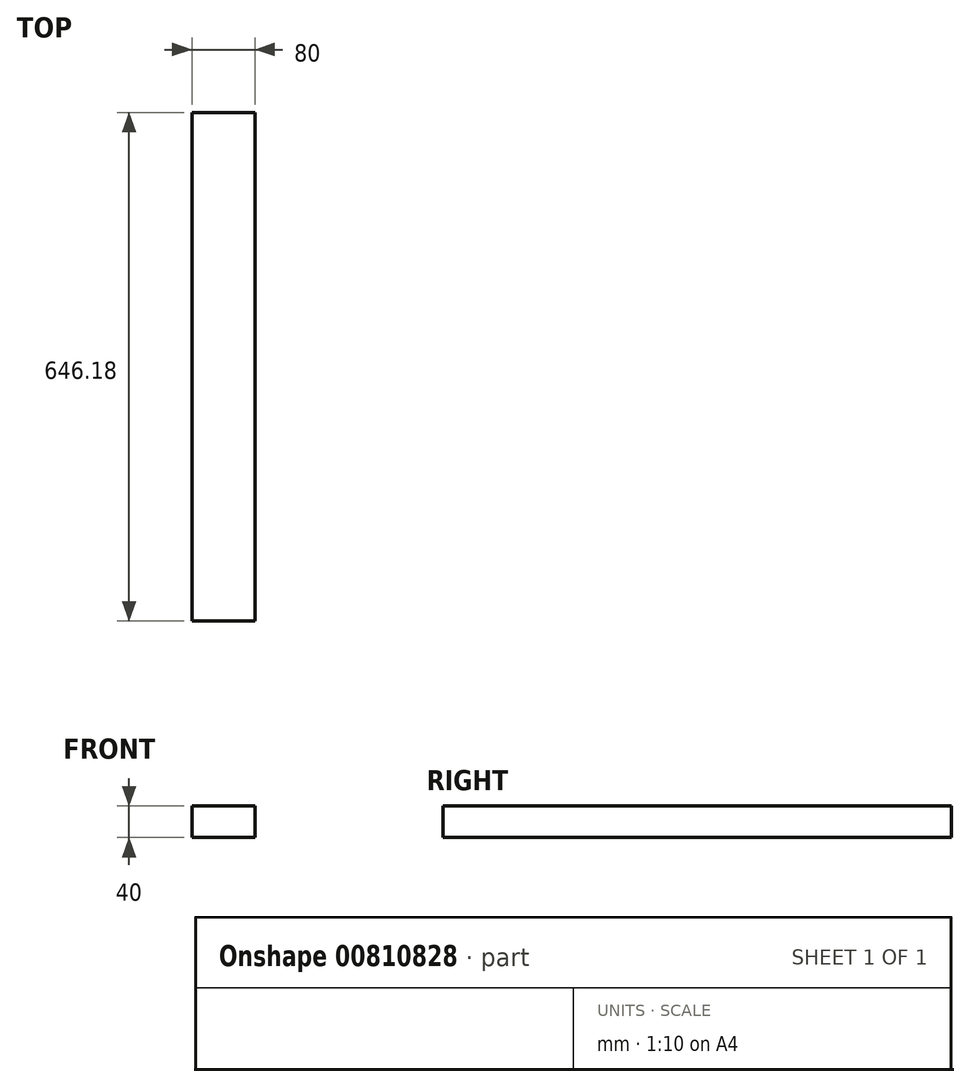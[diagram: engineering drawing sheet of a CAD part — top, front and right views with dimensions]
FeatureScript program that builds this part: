
annotation { "Feature Type Name" : "Feature", "Feature Type Description" : "" }
export const myFeature = defineFeature(function(context is Context, id is Id, definition is map)
    precondition{}
    {
        {
            var Q0;
            Q0=qCreatedBy(makeId("Front.planeOp"),FACE);
            var sketch = newSketch(context, id + "F0", { "sketchPlane" : qUnion([Q0])});
            skLineSegment(sketch, "E0.bottom", {"start": v(-40, 20) * mm, "end": v(40, 20) * mm});
            skLineSegment(sketch, "E0.top", {"start": v(-40, -20) * mm, "end": v(40, -20) * mm});
            skLineSegment(sketch, "E0.left", {"start": v(-40, 20) * mm, "end": v(-40, -20) * mm});
            skLineSegment(sketch, "E0.right", {"start": v(40, 20) * mm, "end": v(40, -20) * mm});
            skPoint(sketch, "E0.middle", {"position": v(0, 0) * mm});
            skSolve(sketch);
        }
        {
            var Q0;
            Q0=makeQuery(id+"F0.imprint","IMPRINT",FACE,{"disambiguationData":[TD([[makeQuery(id+"F0.imprint","IMPRINT",EDGE,{"derivedFrom":sQuery(id+"F0.wireOp",EDGE,"E0.bottom")}),-1.0]])]});
            extrude(context, id + "F1", {"entities" : qUnion([Q0]), "endBound" : BoundingType.SYMMETRIC, "depth" : 646.2 * mm, "offsetDistance" : 25 * mm});
        }
    });
